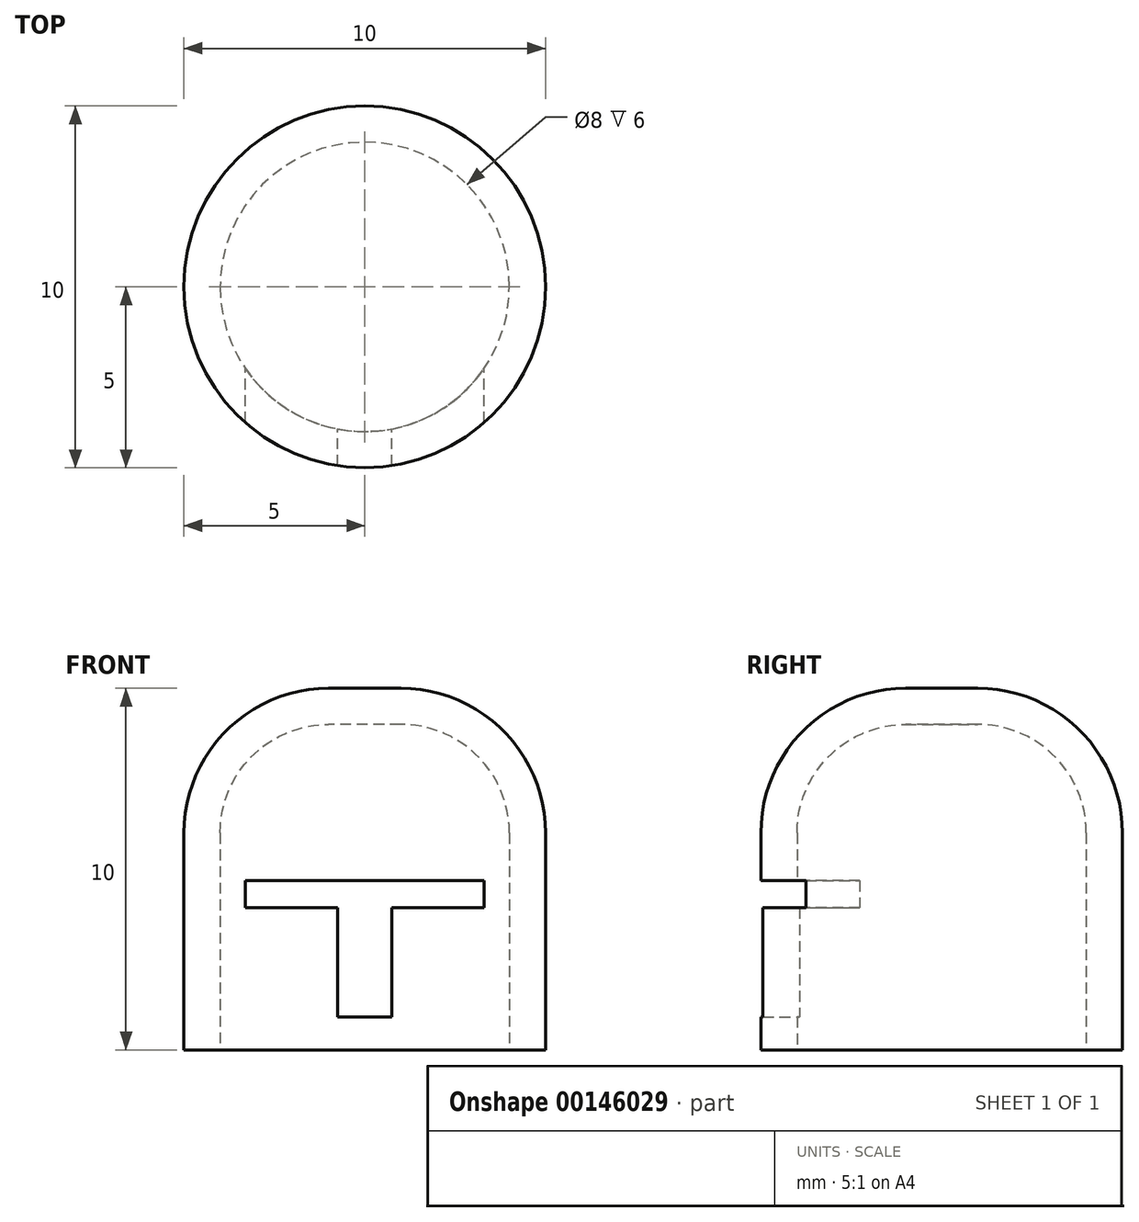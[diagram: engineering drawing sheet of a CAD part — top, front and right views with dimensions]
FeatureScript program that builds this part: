
annotation { "Feature Type Name" : "Feature", "Feature Type Description" : "" }
export const myFeature = defineFeature(function(context is Context, id is Id, definition is map)
    precondition{}
    {
        {
            var Q0;
            Q0=qCreatedBy(makeId("Top.planeOp"),FACE);
            var sketch = newSketch(context, id + "F0", { "sketchPlane" : qUnion([Q0])});
            skCircle(sketch, "E0", {"center": v(0, 0) * mm, "radius": 5 * mm});
            skSolve(sketch);
        }
        {
            var Q0;
            Q0 = qSketchRegion(id + "F0", true);
            extrude(context, id + "F1", {"entities" : qUnion([Q0]), "depth" : 10 * mm});
        }
        {
            var Q0;
            Q0=makeQuery(id+"F1.opExtrude","CAP_FACE",FACE,{"disambiguationData":[OSD([sQuery(id+"F0.wireOp",EDGE,"E0")])],"isStart":false});
            fillet(context, id + "F2", {"entities" : qUnion([Q0]), "radius" : 4 * mm, "tangentPropagation" : true, "allowEdgeOverflow" : false});
        }
        {
            var Q0;
            Q0=makeQuery(id+"F1.opExtrude","CAP_FACE",FACE,{"disambiguationData":[OSD([sQuery(id+"F0.wireOp",EDGE,"E0")])],"isStart":true});
            shell(context, id + "F3", {"entities" : qUnion([Q0]), "thickness" : 1 * mm});
        }
        {
            var Q0;
            Q0=qCreatedBy(makeId("Front.planeOp"),FACE);
            var sketch = newSketch(context, id + "F4", { "sketchPlane" : qUnion([Q0])});
            skLineSegment(sketch, "E1", {"start": v(0, 4.68) * mm, "end": v(3.3, 4.68) * mm});
            skLineSegment(sketch, "E2", {"start": v(3.3, 4.68) * mm, "end": v(3.3, 3.93) * mm});
            skLineSegment(sketch, "E3", {"start": v(3.3, 3.93) * mm, "end": v(0.75, 3.93) * mm});
            skLineSegment(sketch, "E4", {"start": v(0.75, 3.93) * mm, "end": v(0.75, 0.91) * mm});
            skLineSegment(sketch, "E5", {"start": v(0.75, 0.91) * mm, "end": v(-0.75, 0.91) * mm});
            skLineSegment(sketch, "E6", {"start": v(-0.75, 0.91) * mm, "end": v(-0.75, 3.93) * mm});
            skLineSegment(sketch, "E7", {"start": v(-0.75, 3.93) * mm, "end": v(-3.3, 3.93) * mm});
            skLineSegment(sketch, "E8", {"start": v(-3.3, 3.93) * mm, "end": v(-3.3, 4.68) * mm});
            skLineSegment(sketch, "E9", {"start": v(-3.3, 4.68) * mm, "end": v(0, 4.68) * mm});
            skSolve(sketch);
        }
        {
            var Q0;
            Q0 = qSketchRegion(id + "F4", true);
            extrude(context, id + "F5", {"entities" : qUnion([Q0]), "operationType" : NewBodyOperationType.REMOVE, "depth" : 25 * mm});
        }
    });
